# Revit family: Shower_Outlet_Elbow-GROHE-Allure_Brilliant-27708000
name_source: partatom
category: Plumbing Fixtures
units: mm (PartAtom-declared; Revit-internal decimal feet)

## family parameters
Cut with Voids When Loaded = No
Host = Face
OmniClass Number = 23.45.05.14.17
OmniClass Title = Showers
Part Type = Normal
Room Calculation Point = No
Round Connector Dimension = Use Diameter
Shared = Yes

## types (1)
- 27708000
    ADA Compliant = No
    Assembly Code = D2010710
    CW Connection = No
    CWFU = 1.5
    Default Elevation = 0"
    Description = Allure Brilliant Wall Union
    Finish = Metal-Grohe-000-Chrome
    HW Connection = No
    HWFU = 1.5
    Height = 2 1/16"
    IAPMO Compliance = CSA B125.1 and ASME A112.18.1
    Installation Type = Wall Mounted
    Length = 2 5/8"
    Manufacturer = Grohe
    Material = Metal-Grohe-000-Chrome
    Model = 27708000
    Price = Prices may vary. Please consult Manufacturer Representative for most up-to-date price list.
    Product Documentation Link = https://americanstandard.box.com
    Product Page URL = https://www.grohe.ca
    Revised Date = 04/26/2022
    Tempered Connection Diameter = 1/2"
    Tempered Connection Radius = 1/4"
    Tempered Water Connection = Yes
    URL = https://www.grohe.com
    Vent Connection = No
    WFU = 2
    Warranty Documentation Link = https://cdn.cloud.grohe.com
    Waste Connection = No
    Width = 2 1/16"

## geometry (parser evidence)
native form markers: Sweep x3
no freeform markers — native parametric forms only
